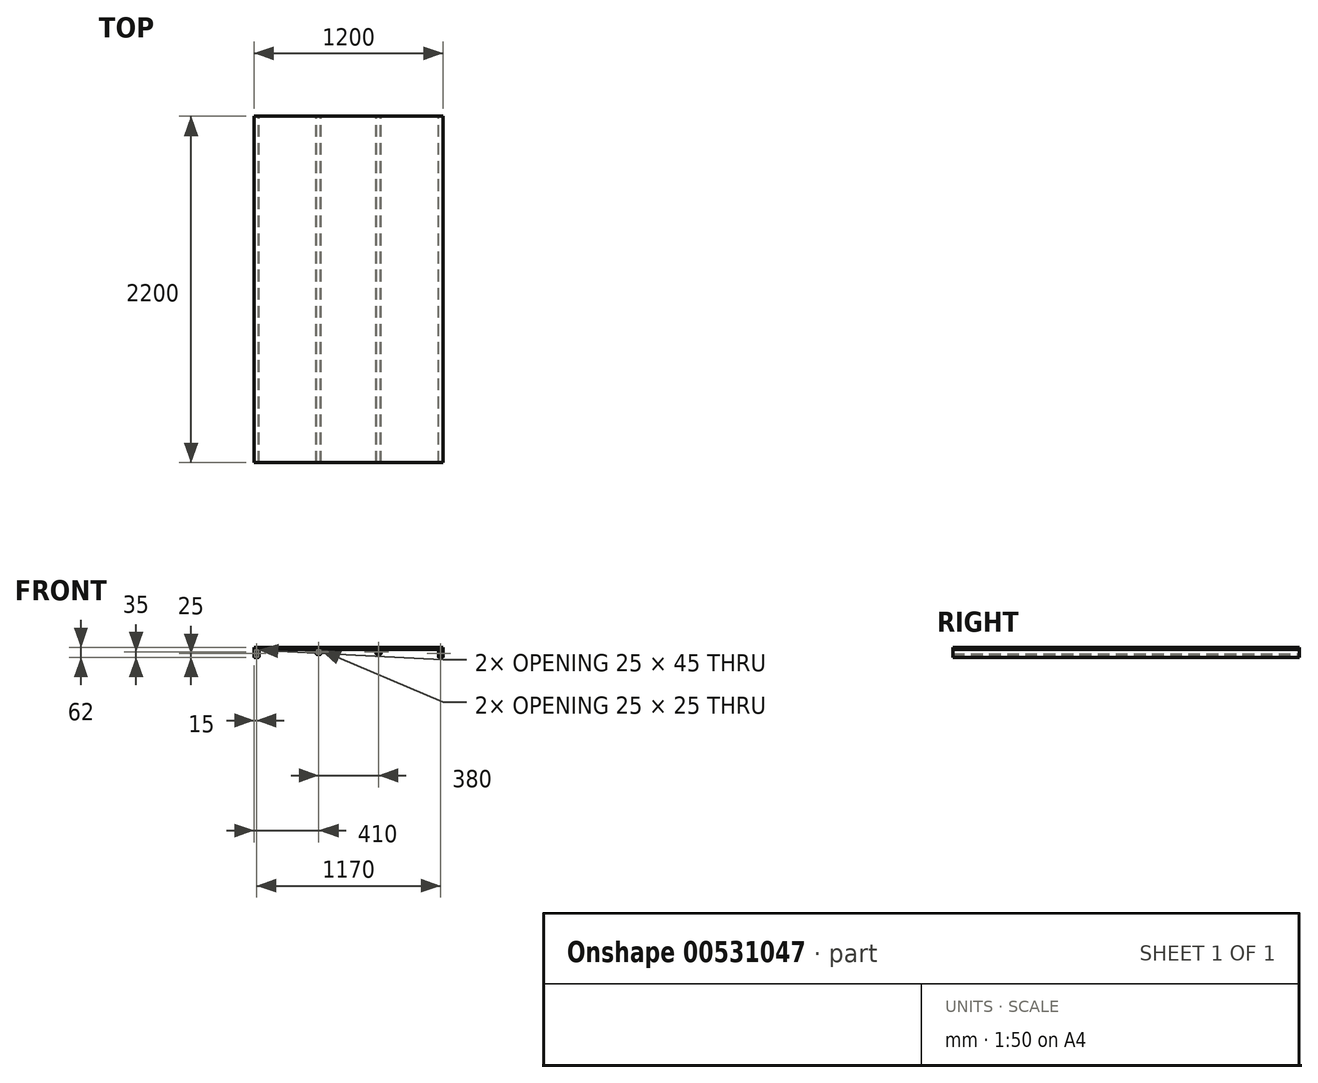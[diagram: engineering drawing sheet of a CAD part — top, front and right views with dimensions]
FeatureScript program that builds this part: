
annotation { "Feature Type Name" : "Feature", "Feature Type Description" : "" }
export const myFeature = defineFeature(function(context is Context, id is Id, definition is map)
    precondition{}
    {
        {
            var Q0;
            Q0=qCreatedBy(makeId("Front.planeOp"),FACE);
            var sketch = newSketch(context, id + "F0", { "sketchPlane" : qUnion([Q0])});
            skLineSegment(sketch, "E0.bottom", {"start": v(-178, 0) * mm, "end": v(-202, 0) * mm});
            skLineSegment(sketch, "E0.top", {"start": v(-178, -30) * mm, "end": v(-202, -30) * mm});
            skLineSegment(sketch, "E0.left", {"start": v(-175, -3) * mm, "end": v(-175, -27) * mm});
            skLineSegment(sketch, "E0.right", {"start": v(-205, -3) * mm, "end": v(-205, -27) * mm});
            skLineSegment(sketch, "E1.bottom", {"start": v(-597, 0) * mm, "end": v(-573, 0) * mm});
            skLineSegment(sketch, "E1.top", {"start": v(-597, -50) * mm, "end": v(-573, -50) * mm});
            skLineSegment(sketch, "E1.left", {"start": v(-600, -3) * mm, "end": v(-600, -47) * mm});
            skLineSegment(sketch, "E1.right", {"start": v(-570, -3) * mm, "end": v(-570, -47) * mm});
            skPoint(sketch, "E2.visualSharp", {"position": v(-600, 0) * mm});
            skArc(sketch, "E2.filletArc", {"start": v(-597, 0) * mm, "mid": v(-599.12, -0.88) * mm, "end": v(-600, -3) * mm});
            skPoint(sketch, "E3.visualSharp", {"position": v(-570, 0) * mm});
            skArc(sketch, "E3.filletArc", {"start": v(-570, -3) * mm, "mid": v(-570.88, -0.88) * mm, "end": v(-573, 0) * mm});
            skPoint(sketch, "E4.visualSharp", {"position": v(-570, -50) * mm});
            skArc(sketch, "E4.filletArc", {"start": v(-573, -50) * mm, "mid": v(-570.88, -49.12) * mm, "end": v(-570, -47) * mm});
            skPoint(sketch, "E5.visualSharp", {"position": v(-600, -50) * mm});
            skArc(sketch, "E5.filletArc", {"start": v(-600, -47) * mm, "mid": v(-599.12, -49.12) * mm, "end": v(-597, -50) * mm});
            skPoint(sketch, "E6.visualSharp", {"position": v(-205, 0) * mm});
            skArc(sketch, "E6.filletArc", {"start": v(-202, 0) * mm, "mid": v(-204.12, -0.88) * mm, "end": v(-205, -3) * mm});
            skPoint(sketch, "E7.visualSharp", {"position": v(-175, 0) * mm});
            skArc(sketch, "E7.filletArc", {"start": v(-175, -3) * mm, "mid": v(-175.88, -0.88) * mm, "end": v(-178, 0) * mm});
            skPoint(sketch, "E8.visualSharp", {"position": v(-175, -30) * mm});
            skArc(sketch, "E8.filletArc", {"start": v(-178, -30) * mm, "mid": v(-175.88, -29.12) * mm, "end": v(-175, -27) * mm});
            skPoint(sketch, "E9.visualSharp", {"position": v(-205, -30) * mm});
            skArc(sketch, "E9.filletArc", {"start": v(-205, -27) * mm, "mid": v(-204.12, -29.12) * mm, "end": v(-202, -30) * mm});
            skLineSegment(sketch, "E10.0", {"start": v(-572.5, -5.8) * mm, "end": v(-572.5, -44.2) * mm});
            skLineSegment(sketch, "E10.1", {"start": v(-594.2, -2.5) * mm, "end": v(-575.8, -2.5) * mm});
            skLineSegment(sketch, "E10.2", {"start": v(-597.5, -5.8) * mm, "end": v(-597.5, -44.2) * mm});
            skLineSegment(sketch, "E10.3", {"start": v(-594.2, -47.5) * mm, "end": v(-575.8, -47.5) * mm});
            skPoint(sketch, "E11.visualSharp", {"position": v(-572.5, -2.5) * mm});
            skArc(sketch, "E11.filletArc", {"start": v(-572.5, -5.8) * mm, "mid": v(-573.47, -3.47) * mm, "end": v(-575.8, -2.5) * mm});
            skPoint(sketch, "E12.visualSharp", {"position": v(-597.5, -2.5) * mm});
            skArc(sketch, "E12.filletArc", {"start": v(-594.2, -2.5) * mm, "mid": v(-596.53, -3.47) * mm, "end": v(-597.5, -5.8) * mm});
            skPoint(sketch, "E13.visualSharp", {"position": v(-572.5, -47.5) * mm});
            skArc(sketch, "E13.filletArc", {"start": v(-575.8, -47.5) * mm, "mid": v(-573.47, -46.53) * mm, "end": v(-572.5, -44.2) * mm});
            skPoint(sketch, "E14.visualSharp", {"position": v(-597.5, -47.5) * mm});
            skArc(sketch, "E14.filletArc", {"start": v(-597.5, -44.2) * mm, "mid": v(-596.53, -46.53) * mm, "end": v(-594.2, -47.5) * mm});
            skLineSegment(sketch, "E15.0", {"start": v(-177.5, -5) * mm, "end": v(-177.5, -25) * mm});
            skLineSegment(sketch, "E15.1", {"start": v(-180, -2.5) * mm, "end": v(-200, -2.5) * mm});
            skLineSegment(sketch, "E15.2", {"start": v(-202.5, -5) * mm, "end": v(-202.5, -25) * mm});
            skLineSegment(sketch, "E15.3", {"start": v(-180, -27.5) * mm, "end": v(-200, -27.5) * mm});
            skPoint(sketch, "E16.visualSharp", {"position": v(-202.5, -2.5) * mm});
            skArc(sketch, "E16.filletArc", {"start": v(-200, -2.5) * mm, "mid": v(-201.77, -3.23) * mm, "end": v(-202.5, -5) * mm});
            skPoint(sketch, "E17.visualSharp", {"position": v(-177.5, -2.5) * mm});
            skArc(sketch, "E17.filletArc", {"start": v(-177.5, -5) * mm, "mid": v(-178.23, -3.23) * mm, "end": v(-180, -2.5) * mm});
            skPoint(sketch, "E18.visualSharp", {"position": v(-177.5, -27.5) * mm});
            skArc(sketch, "E18.filletArc", {"start": v(-180, -27.5) * mm, "mid": v(-178.23, -26.77) * mm, "end": v(-177.5, -25) * mm});
            skPoint(sketch, "E19.visualSharp", {"position": v(-202.5, -27.5) * mm});
            skArc(sketch, "E19.filletArc", {"start": v(-202.5, -25) * mm, "mid": v(-201.77, -26.77) * mm, "end": v(-200, -27.5) * mm});
            skPoint(sketch, "E20", {"position": v(-190, -30) * mm});
            skLineSegment(sketch, "E21", {"start": v(0, 0) * mm, "end": v(0, 195.02) * mm, "construction": true});
            skArc(sketch, "E22.MirrorCS", {"start": v(178, -30) * mm, "mid": v(175.88, -29.12) * mm, "end": v(175, -27) * mm});
            skArc(sketch, "E23.MirrorCS", {"start": v(205, -27) * mm, "mid": v(204.12, -29.12) * mm, "end": v(202, -30) * mm});
            skLineSegment(sketch, "E24.MirrorCS", {"start": v(178, -30) * mm, "end": v(202, -30) * mm});
            skArc(sketch, "E25.MirrorCS", {"start": v(202.5, -25) * mm, "mid": v(201.77, -26.77) * mm, "end": v(200, -27.5) * mm});
            skArc(sketch, "E26.MirrorCS", {"start": v(180, -27.5) * mm, "mid": v(178.23, -26.77) * mm, "end": v(177.5, -25) * mm});
            skLineSegment(sketch, "E27.MirrorCS", {"start": v(180, -27.5) * mm, "end": v(200, -27.5) * mm});
            skLineSegment(sketch, "E28.MirrorCS", {"start": v(202.5, -5) * mm, "end": v(202.5, -25) * mm});
            skLineSegment(sketch, "E29.MirrorCS", {"start": v(205, -3) * mm, "end": v(205, -27) * mm});
            skArc(sketch, "E30.MirrorCS", {"start": v(200, -2.5) * mm, "mid": v(201.77, -3.23) * mm, "end": v(202.5, -5) * mm});
            skArc(sketch, "E31.MirrorCS", {"start": v(202, 0) * mm, "mid": v(204.12, -0.88) * mm, "end": v(205, -3) * mm});
            skArc(sketch, "E32.MirrorCS", {"start": v(175, -3) * mm, "mid": v(175.88, -0.88) * mm, "end": v(178, 0) * mm});
            skLineSegment(sketch, "E33.MirrorCS", {"start": v(178, 0) * mm, "end": v(202, 0) * mm});
            skLineSegment(sketch, "E34.MirrorCS", {"start": v(175, -3) * mm, "end": v(175, -27) * mm});
            skArc(sketch, "E35.MirrorCS", {"start": v(177.5, -5) * mm, "mid": v(178.23, -3.23) * mm, "end": v(180, -2.5) * mm});
            skArc(sketch, "E36.MirrorCS", {"start": v(597, 0) * mm, "mid": v(599.12, -0.88) * mm, "end": v(600, -3) * mm});
            skArc(sketch, "E37.MirrorCS", {"start": v(594.2, -2.5) * mm, "mid": v(596.53, -3.47) * mm, "end": v(597.5, -5.8) * mm});
            skLineSegment(sketch, "E38.MirrorCS", {"start": v(180, -2.5) * mm, "end": v(200, -2.5) * mm});
            skLineSegment(sketch, "E39.MirrorCS", {"start": v(594.2, -47.5) * mm, "end": v(575.8, -47.5) * mm});
            skArc(sketch, "E40.MirrorCS", {"start": v(570, -3) * mm, "mid": v(570.88, -0.88) * mm, "end": v(573, 0) * mm});
            skLineSegment(sketch, "E41.MirrorCS", {"start": v(597, 0) * mm, "end": v(573, 0) * mm});
            skArc(sketch, "E42.MirrorCS", {"start": v(600, -47) * mm, "mid": v(599.12, -49.12) * mm, "end": v(597, -50) * mm});
            skLineSegment(sketch, "E43.MirrorCS", {"start": v(594.2, -2.5) * mm, "end": v(575.8, -2.5) * mm});
            skLineSegment(sketch, "E44.MirrorCS", {"start": v(597, -50) * mm, "end": v(573, -50) * mm});
            skLineSegment(sketch, "E45.MirrorCS", {"start": v(177.5, -5) * mm, "end": v(177.5, -25) * mm});
            skArc(sketch, "E46.MirrorCS", {"start": v(573, -50) * mm, "mid": v(570.88, -49.12) * mm, "end": v(570, -47) * mm});
            skArc(sketch, "E47.MirrorCS", {"start": v(572.5, -5.8) * mm, "mid": v(573.47, -3.47) * mm, "end": v(575.8, -2.5) * mm});
            skArc(sketch, "E48.MirrorCS", {"start": v(575.8, -47.5) * mm, "mid": v(573.47, -46.53) * mm, "end": v(572.5, -44.2) * mm});
            skArc(sketch, "E49.MirrorCS", {"start": v(597.5, -44.2) * mm, "mid": v(596.53, -46.53) * mm, "end": v(594.2, -47.5) * mm});
            skPoint(sketch, "E50.MirrorP", {"position": v(202.5, -2.5) * mm});
            skLineSegment(sketch, "E51.MirrorCS", {"start": v(572.5, -5.8) * mm, "end": v(572.5, -44.2) * mm});
            skLineSegment(sketch, "E52.MirrorCS", {"start": v(570, -3) * mm, "end": v(570, -47) * mm});
            skPoint(sketch, "E53.MirrorP", {"position": v(177.5, -27.5) * mm});
            skPoint(sketch, "E54.MirrorP", {"position": v(177.5, -2.5) * mm});
            skPoint(sketch, "E55.MirrorP", {"position": v(202.5, -27.5) * mm});
            skLineSegment(sketch, "E56.MirrorCS", {"start": v(600, -3) * mm, "end": v(600, -47) * mm});
            skLineSegment(sketch, "E57.MirrorCS", {"start": v(597.5, -5.8) * mm, "end": v(597.5, -44.2) * mm});
            skPoint(sketch, "E58.MirrorP", {"position": v(205, 0) * mm});
            skPoint(sketch, "E59.MirrorP", {"position": v(570, 0) * mm});
            skPoint(sketch, "E60.MirrorP", {"position": v(597.5, -2.5) * mm});
            skPoint(sketch, "E61.MirrorP", {"position": v(600, 0) * mm});
            skPoint(sketch, "E62.MirrorP", {"position": v(572.5, -47.5) * mm});
            skPoint(sketch, "E63.MirrorP", {"position": v(570, -50) * mm});
            skPoint(sketch, "E64.MirrorP", {"position": v(597.5, -47.5) * mm});
            skPoint(sketch, "E65.MirrorP", {"position": v(600, -50) * mm});
            skPoint(sketch, "E66.MirrorP", {"position": v(205, -30) * mm});
            skPoint(sketch, "E67.MirrorP", {"position": v(175, 0) * mm});
            skPoint(sketch, "E68.MirrorP", {"position": v(175, -30) * mm});
            skPoint(sketch, "E69.MirrorP", {"position": v(190, -30) * mm});
            skPoint(sketch, "E70.MirrorP", {"position": v(572.5, -2.5) * mm});
            skSolve(sketch);
        }
        {
            var Q0;
            Q0 = qSketchRegion(id + "F0", true);
            extrude(context, id + "F1", {"entities" : qUnion([Q0]), "depth" : 2200 * mm, "offsetDistance" : 25 * mm});
        }
        {
            var Q0;
            Q0=makeQuery(id+"F1.opExtrude","SWEPT_FACE",FACE,{"disambiguationData":[OSD([sQuery(id+"F0.wireOp",EDGE,"E1.bottom")])]});
            var sketch = newSketch(context, id + "F2", { "sketchPlane" : qUnion([Q0])});
            skLineSegment(sketch, "E71.bottom", {"start": v(-600, -2200) * mm, "end": v(600, -2200) * mm});
            skLineSegment(sketch, "E71.top", {"start": v(-600, 0) * mm, "end": v(600, 0) * mm});
            skLineSegment(sketch, "E71.left", {"start": v(-600, -2200) * mm, "end": v(-600, 0) * mm});
            skLineSegment(sketch, "E71.right", {"start": v(600, -2200) * mm, "end": v(600, 0) * mm});
            skSolve(sketch);
        }
        {
            var Q0;
            Q0 = qSketchRegion(id + "F2", true);
            extrude(context, id + "F3", {"entities" : qUnion([Q0]), "depth" : 12 * mm, "offsetDistance" : 25 * mm});
        }
    });
